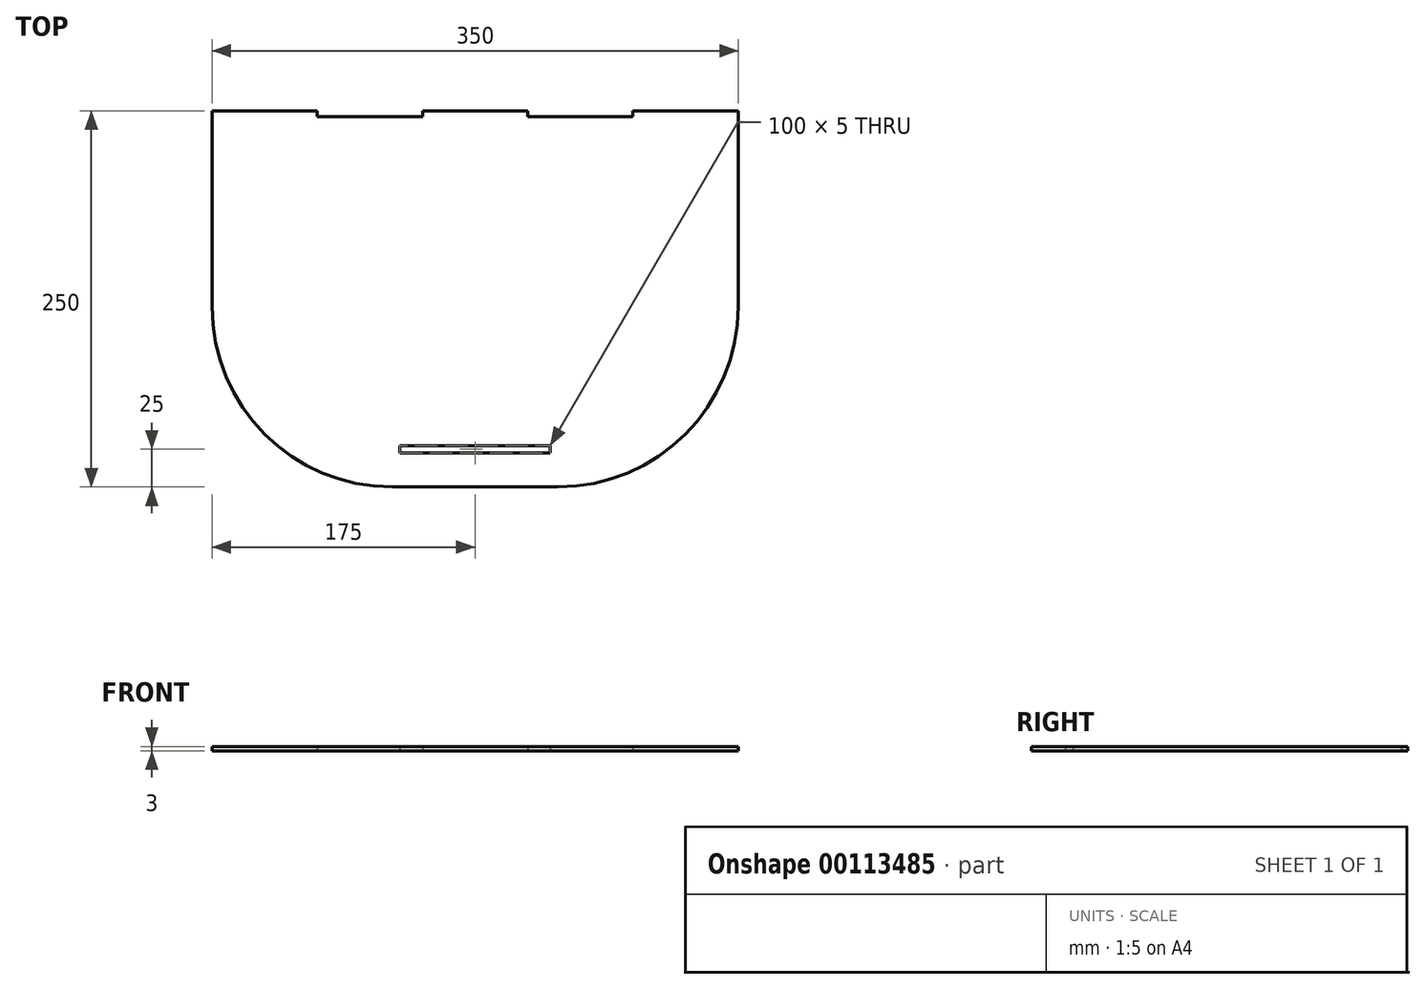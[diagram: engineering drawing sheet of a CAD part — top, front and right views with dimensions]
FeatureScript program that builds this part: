
annotation { "Feature Type Name" : "Feature", "Feature Type Description" : "" }
export const myFeature = defineFeature(function(context is Context, id is Id, definition is map)
    precondition{}
    {
        {
            var Q0;
            Q0=qCreatedBy(makeId("Top.planeOp"),FACE);
            var sketch = newSketch(context, id + "F0", { "sketchPlane" : qUnion([Q0])});
            skLineSegment(sketch, "E0.bottom", {"start": v(0, 0) * mm, "end": v(350, 0) * mm});
            skLineSegment(sketch, "E0.top", {"start": v(0, 250) * mm, "end": v(70, 250) * mm});
            skLineSegment(sketch, "E0.left", {"start": v(0, 0) * mm, "end": v(0, 250) * mm});
            skLineSegment(sketch, "E0.right", {"start": v(350, 0) * mm, "end": v(350, 250) * mm});
            skLineSegment(sketch, "E1", {"start": v(175, 250) * mm, "end": v(175, 0) * mm, "construction": true});
            skLineSegment(sketch, "E2", {"start": v(0, 125) * mm, "end": v(350, 125) * mm, "construction": true});
            skLineSegment(sketch, "E3.bottom", {"start": v(210, 246) * mm, "end": v(140, 246) * mm});
            skLineSegment(sketch, "E3.top", {"start": v(210, 250) * mm, "end": v(140, 250) * mm});
            skLineSegment(sketch, "E3.left", {"start": v(210, 246) * mm, "end": v(210, 250) * mm});
            skLineSegment(sketch, "E3.right", {"start": v(140, 246) * mm, "end": v(140, 250) * mm});
            skPoint(sketch, "E3.middle", {"position": v(175, 248) * mm});
            skLineSegment(sketch, "E4.bottom", {"start": v(70, 246) * mm, "end": v(0, 246) * mm});
            skLineSegment(sketch, "E4.top", {"start": v(70, 250) * mm, "end": v(0, 250) * mm});
            skLineSegment(sketch, "E4.left", {"start": v(70, 246) * mm, "end": v(70, 250) * mm});
            skLineSegment(sketch, "E4.right", {"start": v(0, 246) * mm, "end": v(0, 250) * mm});
            skPoint(sketch, "E4.middle", {"position": v(35, 248) * mm});
            skLineSegment(sketch, "E5.MirrorCS", {"start": v(280, 246) * mm, "end": v(350, 246) * mm});
            skLineSegment(sketch, "E6.MirrorCS", {"start": v(280, 246) * mm, "end": v(280, 250) * mm});
            skLineSegment(sketch, "E7.MirrorCS", {"start": v(350, 246) * mm, "end": v(350, 250) * mm});
            skLineSegment(sketch, "E8", {"start": v(70, 246) * mm, "end": v(140, 246) * mm});
            skLineSegment(sketch, "E9", {"start": v(210, 246) * mm, "end": v(280, 246) * mm});
            skLineSegment(sketch, "E10.trimOffspring", {"start": v(140, 250) * mm, "end": v(210, 250) * mm});
            skLineSegment(sketch, "E11.trimOffspring", {"start": v(280, 250) * mm, "end": v(350, 250) * mm});
            skLineSegment(sketch, "E12.bottom", {"start": v(225, 22.5) * mm, "end": v(125, 22.5) * mm});
            skLineSegment(sketch, "E12.top", {"start": v(225, 27.5) * mm, "end": v(125, 27.5) * mm});
            skLineSegment(sketch, "E12.left", {"start": v(225, 22.5) * mm, "end": v(225, 27.5) * mm});
            skLineSegment(sketch, "E12.right", {"start": v(125, 22.5) * mm, "end": v(125, 27.5) * mm});
            skPoint(sketch, "E12.middle", {"position": v(175, 25) * mm});
            skSolve(sketch);
        }
        {
            var Q0;
            Q0=makeQuery(id+"F0.imprint","IMPRINT",FACE,{"disambiguationData":[TD([[makeQuery(id+"F0.imprint","IMPRINT",EDGE,{"derivedFrom":sQuery(id+"F0.wireOp",EDGE,"E0.bottom")}),1.0]])]});
            var Q1;
            Q1=makeQuery(id+"F0.imprint","IMPRINT",FACE,{"disambiguationData":[TD([[makeQuery(id+"F0.imprint","IMPRINT",EDGE,{"derivedFrom":sQuery(id+"F0.wireOp",EDGE,"E3.bottom")}),-1.0]])]});
            var Q2;
            Q2=makeQuery(id+"F0.imprint","IMPRINT",FACE,{"disambiguationData":[TD([[makeQuery(id+"F0.imprint","IMPRINT",EDGE,{"derivedFrom":sQuery(id+"F0.wireOp",EDGE,"E5.MirrorCS")}),1.0]])]});
            var Q3;
            Q3=makeQuery(id+"F0.imprint","IMPRINT",FACE,{"disambiguationData":[TD([[makeQuery(id+"F0.imprint","IMPRINT",EDGE,{"derivedFrom":sQuery(id+"F0.wireOp",EDGE,"E4.bottom")}),-1.0]])]});
            extrude(context, id + "F1", {"entities" : qUnion([Q0, Q1, Q2, Q3]), "depth" : 3 * mm});
        }
        {
            var Q0;
            Q0=makeQuery(id+"F1.opExtrude","SWEPT_EDGE",EDGE,{"disambiguationData":[OSD([sQuery(id+"F0.wireOp",EDGE,"E0.bottom"),sQuery(id+"F0.wireOp",EDGE,"E0.left")])]});
            var Q1;
            Q1=makeQuery(id+"F1.opExtrude","SWEPT_EDGE",EDGE,{"disambiguationData":[OSD([sQuery(id+"F0.wireOp",EDGE,"E0.bottom"),sQuery(id+"F0.wireOp",EDGE,"E0.right")])]});
            fillet(context, id + "F2", {"entities" : qUnion([Q0, Q1]), "radius" : 120 * mm, "tangentPropagation" : true, "allowEdgeOverflow" : false});
        }
    });
